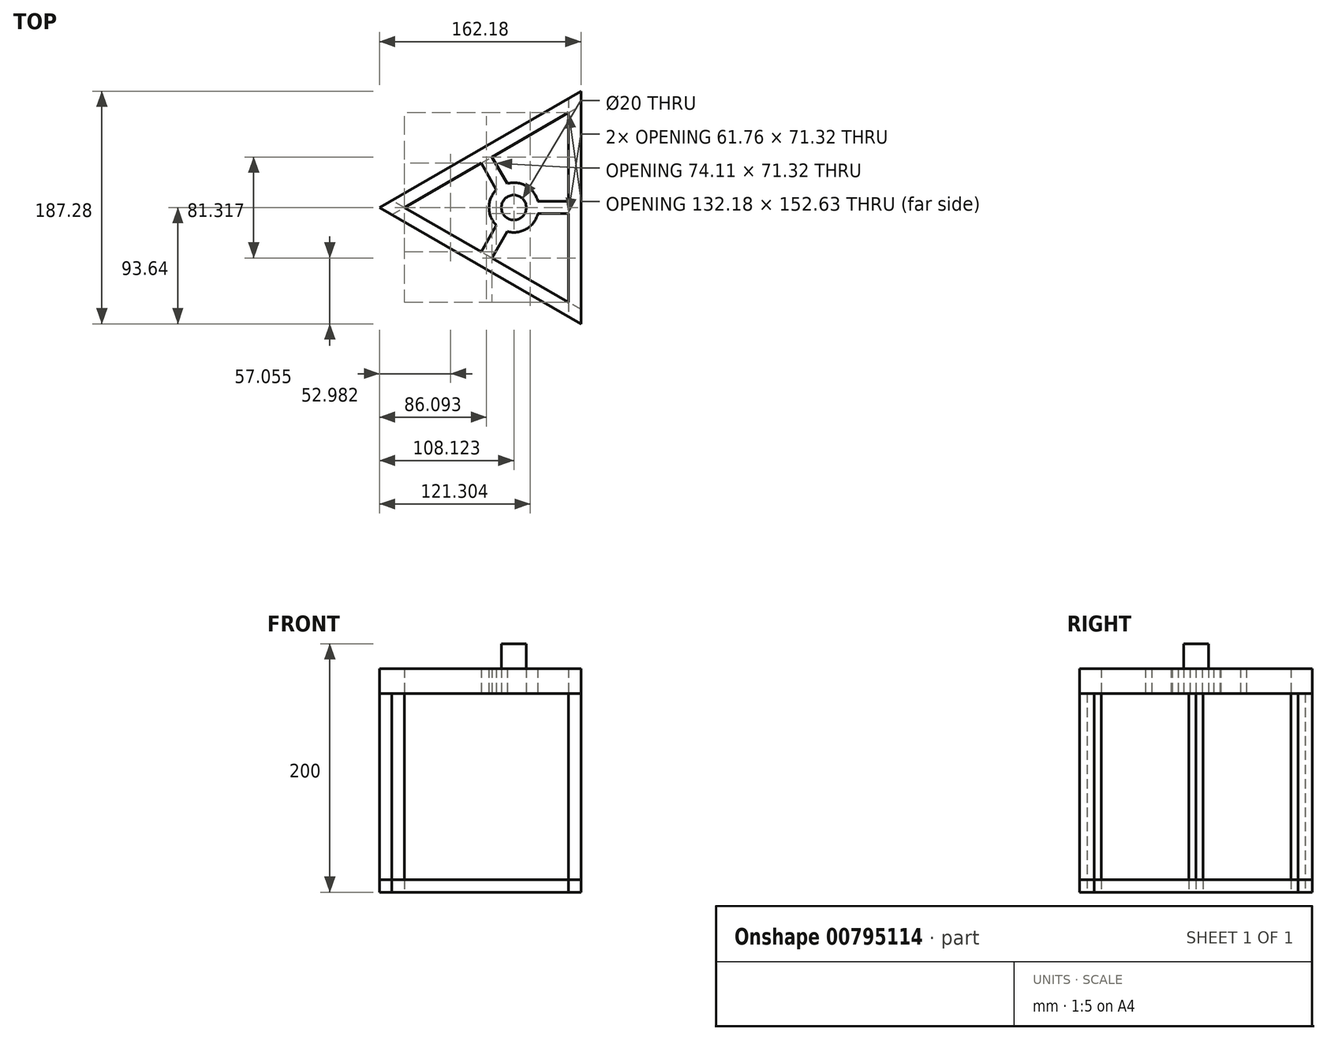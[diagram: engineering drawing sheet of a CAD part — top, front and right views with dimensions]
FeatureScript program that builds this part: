
annotation { "Feature Type Name" : "Feature", "Feature Type Description" : "" }
export const myFeature = defineFeature(function(context is Context, id is Id, definition is map)
    precondition{}
    {
        {
            var Q0;
            Q0=qCreatedBy(makeId("Top.planeOp"),FACE);
            var sketch = newSketch(context, id + "F0", { "sketchPlane" : qUnion([Q0])});
            skCircle(sketch, "E0.cCircle", {"center": v(0, 0) * mm, "radius": 54.06 * mm, "construction": true});
            skLineSegment(sketch, "E0.0", {"start": v(54.06, 93.64) * mm, "end": v(54.06, -93.64) * mm});
            skLineSegment(sketch, "E0.1", {"start": v(54.06, -93.64) * mm, "end": v(-108.12, 0) * mm});
            skLineSegment(sketch, "E0.2", {"start": v(-108.12, 0) * mm, "end": v(54.06, 93.64) * mm});
            skPoint(sketch, "E0.0.midPoint", {"position": v(54.06, 0) * mm});
            skLineSegment(sketch, "E1.0", {"start": v(44.06, 87.86) * mm, "end": v(44.06, -87.86) * mm});
            skLineSegment(sketch, "E2.0", {"start": v(-98.12, -5.77) * mm, "end": v(54.06, 82.1) * mm});
            skLineSegment(sketch, "E3.0", {"start": v(54.06, -82.1) * mm, "end": v(-98.12, 5.77) * mm});
            skCircle(sketch, "E4", {"center": v(0, 0) * mm, "radius": 8.55 * mm});
            skSolve(sketch);
        }
        {
            var Q0;
            {var subQ0=sQuery(id+"F0.wireOp",EDGE,"E2.0");var subQ1=sQuery(id+"F0.wireOp",EDGE,"E0.0");var subQ2=makeQuery(id+"F0.imprint","INTERSECT",VERTEX,{"derivedFrom":[subQ1,subQ0]});Q0=makeQuery(id+"F0.imprint","IMPRINT",FACE,{"disambiguationData":[TD([[makeQuery(id+"F0.imprint","IMPRINT",EDGE,{"disambiguationData":[TD([[subQ2,-1.0]])],"derivedFrom":subQ1}),-1.0]])]});}
            var Q1;
            {var subQ0=sQuery(id+"F0.wireOp",EDGE,"E0.2");var subQ1=sQuery(id+"F0.wireOp",EDGE,"E0.1");var subQ2=makeQuery(id+"F0.imprint","INTERSECT",VERTEX,{"derivedFrom":[subQ1,subQ0]});Q1=makeQuery(id+"F0.imprint","IMPRINT",FACE,{"disambiguationData":[TD([[makeQuery(id+"F0.imprint","IMPRINT",EDGE,{"disambiguationData":[TD([[subQ2,1.0]])],"derivedFrom":subQ1}),-1.0]])]});}
            var Q2;
            {var subQ0=sQuery(id+"F0.wireOp",EDGE,"E0.1");var subQ1=sQuery(id+"F0.wireOp",EDGE,"E0.0");var subQ2=makeQuery(id+"F0.imprint","INTERSECT",VERTEX,{"derivedFrom":[subQ1,subQ0]});Q2=makeQuery(id+"F0.imprint","IMPRINT",FACE,{"disambiguationData":[TD([[makeQuery(id+"F0.imprint","IMPRINT",EDGE,{"disambiguationData":[TD([[subQ2,1.0]])],"derivedFrom":subQ1}),-1.0]])]});}
            var Q3;
            {var subQ0=sQuery(id+"F0.wireOp",EDGE,"E1.0");var subQ1=sQuery(id+"F0.wireOp",EDGE,"E0.2");var subQ2=makeQuery(id+"F0.imprint","INTERSECT",VERTEX,{"derivedFrom":[subQ1,subQ0]});Q3=makeQuery(id+"F0.imprint","IMPRINT",FACE,{"disambiguationData":[TD([[makeQuery(id+"F0.imprint","IMPRINT",EDGE,{"disambiguationData":[TD([[subQ2,1.0]])],"derivedFrom":subQ1}),-1.0]])]});}
            var Q4;
            {var subQ0=sQuery(id+"F0.wireOp",EDGE,"E0.2");var subQ1=sQuery(id+"F0.wireOp",EDGE,"E0.0");var subQ2=makeQuery(id+"F0.imprint","INTERSECT",VERTEX,{"derivedFrom":[subQ1,subQ0]});Q4=makeQuery(id+"F0.imprint","IMPRINT",FACE,{"disambiguationData":[TD([[makeQuery(id+"F0.imprint","IMPRINT",EDGE,{"disambiguationData":[TD([[subQ2,-1.0]])],"derivedFrom":subQ1}),-1.0]])]});}
            var Q5;
            {var subQ0=sQuery(id+"F0.wireOp",EDGE,"E1.0");var subQ1=sQuery(id+"F0.wireOp",EDGE,"E0.1");var subQ2=makeQuery(id+"F0.imprint","INTERSECT",VERTEX,{"derivedFrom":[subQ1,subQ0]});Q5=makeQuery(id+"F0.imprint","IMPRINT",FACE,{"disambiguationData":[TD([[makeQuery(id+"F0.imprint","IMPRINT",EDGE,{"disambiguationData":[TD([[subQ2,-1.0]])],"derivedFrom":subQ1}),-1.0]])]});}
            extrude(context, id + "F1", {"entities" : qUnion([Q0, Q1, Q2, Q3, Q4, Q5]), "depth" : 10 * mm, "offsetDistance" : 25 * mm});
        }
        {
            var Q0;
            Q0=makeQuery(id+"F0.imprint","IMPRINT",FACE,{"disambiguationData":[TD([[makeQuery(id+"F0.imprint","IMPRINT",EDGE,{"derivedFrom":sQuery(id+"F0.wireOp",EDGE,"E4")}),-1.0]])]});
            var sketch = newSketch(context, id + "F2", { "sketchPlane" : qUnion([Q0])});
            skLineSegment(sketch, "E5.0", {"start": v(48.05, 93.64) * mm, "end": v(48.05, 82.1) * mm});
            skLineSegment(sketch, "E5.1", {"start": v(48.05, -93.64) * mm, "end": v(38.05, -87.86) * mm});
            skLineSegment(sketch, "E5.2", {"start": v(-114.13, 0) * mm, "end": v(-104.13, 5.77) * mm});
            skPoint(sketch, "E5.0.midPoint", {"position": v(48.05, 0) * mm});
            skLineSegment(sketch, "E6.0", {"start": v(38.05, 87.86) * mm, "end": v(38.05, 76.32) * mm});
            skLineSegment(sketch, "E7.0", {"start": v(-104.13, -5.77) * mm, "end": v(-94.13, 0) * mm});
            skLineSegment(sketch, "E8.0", {"start": v(48.05, -82.1) * mm, "end": v(38.05, -76.32) * mm});
            skLineSegment(sketch, "E9.trimOffspring", {"start": v(-94.13, 0) * mm, "end": v(-104.13, 5.77) * mm});
            skLineSegment(sketch, "E10.trimOffspring", {"start": v(-104.13, -5.77) * mm, "end": v(-114.13, 0) * mm});
            skLineSegment(sketch, "E11.trimOffspring", {"start": v(38.05, 76.32) * mm, "end": v(48.05, 82.1) * mm});
            skLineSegment(sketch, "E12.trimOffspring", {"start": v(38.05, 87.86) * mm, "end": v(48.05, 93.64) * mm});
            skLineSegment(sketch, "E13.trimOffspring", {"start": v(38.05, -76.32) * mm, "end": v(38.05, -87.86) * mm});
            skLineSegment(sketch, "E14.trimOffspring", {"start": v(48.05, -82.1) * mm, "end": v(48.05, -93.64) * mm});
            skPoint(sketch, "E5.cCircle.center.orphan", {"position": v(-6, 0) * mm});
            skSolve(sketch);
        }
        {
            var Q0;
            Q0=makeQuery(id+"F2.imprint","IMPRINT",FACE,{"disambiguationData":[TD([[makeQuery(id+"F2.imprint","IMPRINT",EDGE,{"derivedFrom":sQuery(id+"F2.wireOp",EDGE,"E5.0")}),-1.0]])]});
            var Q1;
            Q1=makeQuery(id+"F2.imprint","IMPRINT",FACE,{"disambiguationData":[TD([[makeQuery(id+"F2.imprint","IMPRINT",EDGE,{"derivedFrom":sQuery(id+"F2.wireOp",EDGE,"E5.1")}),-1.0]])]});
            var Q2;
            Q2=makeQuery(id+"F2.imprint","IMPRINT",FACE,{"disambiguationData":[TD([[makeQuery(id+"F2.imprint","IMPRINT",EDGE,{"derivedFrom":sQuery(id+"F2.wireOp",EDGE,"E5.2")}),-1.0]])]});
            extrude(context, id + "F3", {"entities" : qUnion([Q0, Q1, Q2]), "depth" : 160 * mm, "offsetDistance" : 25 * mm});
        }
        {
            var Q0;
            Q0=qCreatedBy(makeId("Top.planeOp"),FACE);
            var sketch = newSketch(context, id + "F4", { "sketchPlane" : qUnion([Q0])});
            skCircle(sketch, "E15.cCircle", {"center": v(-6, 0) * mm, "radius": 54.06 * mm, "construction": true});
            skLineSegment(sketch, "E15.0", {"start": v(48.05, 93.64) * mm, "end": v(48.05, -93.64) * mm});
            skLineSegment(sketch, "E15.1", {"start": v(48.05, -93.64) * mm, "end": v(-114.13, 0) * mm});
            skLineSegment(sketch, "E15.2", {"start": v(-114.13, 0) * mm, "end": v(48.05, 93.64) * mm});
            skPoint(sketch, "E15.0.midPoint", {"position": v(48.05, 0) * mm});
            skLineSegment(sketch, "E16.0", {"start": v(38.05, 87.86) * mm, "end": v(38.05, -87.86) * mm});
            skLineSegment(sketch, "E17.0", {"start": v(-104.13, -5.77) * mm, "end": v(48.05, 82.1) * mm});
            skLineSegment(sketch, "E18.0", {"start": v(48.05, -82.1) * mm, "end": v(-104.13, 5.77) * mm});
            skCircle(sketch, "E19", {"center": v(-6, 0) * mm, "radius": 10 * mm});
            skCircle(sketch, "E20.0", {"center": v(-6, 0) * mm, "radius": 20 * mm});
            skLineSegment(sketch, "E21.0", {"start": v(13.36, -5) * mm, "end": v(38.05, -5) * mm});
            skLineSegment(sketch, "E22.0", {"start": v(13.36, 5) * mm, "end": v(38.05, 5) * mm});
            skLineSegment(sketch, "E23.0", {"start": v(-20.02, -14.27) * mm, "end": v(-32.37, -35.66) * mm});
            skPoint(sketch, "E24.orphan", {"position": v(-28.04, 38.16) * mm});
            skLineSegment(sketch, "E25.trimOffspring", {"start": v(-20.02, 14.27) * mm, "end": v(-32.37, 35.66) * mm});
            skLineSegment(sketch, "E26.trimOffspring", {"start": v(-11.36, 19.27) * mm, "end": v(-23.7, 40.66) * mm});
            skLineSegment(sketch, "E27.trimOffspring", {"start": v(-11.36, -19.27) * mm, "end": v(-23.7, -40.66) * mm});
            skPoint(sketch, "E28.end.orphan", {"position": v(-28.04, -38.16) * mm});
            skPoint(sketch, "E29.end.orphan", {"position": v(38.05, 0) * mm});
            skSolve(sketch);
        }
        {
            var Q0;
            Q0=makeQuery(id+"F4.imprint","IMPRINT",FACE,{"disambiguationData":[TD([[makeQuery(id+"F4.imprint","IMPRINT",EDGE,{"derivedFrom":sQuery(id+"F4.wireOp",EDGE,"E19")}),1.0]])]});
            extrude(context, id + "F5", {"entities" : qUnion([Q0]), "depth" : 40 * mm, "offsetDistance" : 25 * mm});
        }
        {
            var Q0;
            {var subQ0=sQuery(id+"F4.wireOp",EDGE,"E21.0");Q0=makeQuery(id+"F4.imprint","IMPRINT",FACE,{"disambiguationData":[TD([[makeQuery(id+"F4.imprint","IMPRINT",EDGE,{"derivedFrom":subQ0}),1.0]])]});}
            var Q1;
            {var subQ0=sQuery(id+"F4.wireOp",EDGE,"E15.2");var subQ1=sQuery(id+"F4.wireOp",EDGE,"E15.1");var subQ2=makeQuery(id+"F4.imprint","INTERSECT",VERTEX,{"derivedFrom":[subQ1,subQ0]});Q1=makeQuery(id+"F4.imprint","IMPRINT",FACE,{"disambiguationData":[TD([[makeQuery(id+"F4.imprint","IMPRINT",EDGE,{"disambiguationData":[TD([[subQ2,1.0]])],"derivedFrom":subQ1}),-1.0]])]});}
            var Q2;
            {var subQ0=sQuery(id+"F4.wireOp",EDGE,"E15.1");var subQ1=sQuery(id+"F4.wireOp",EDGE,"E15.0");var subQ2=makeQuery(id+"F4.imprint","INTERSECT",VERTEX,{"derivedFrom":[subQ1,subQ0]});Q2=makeQuery(id+"F4.imprint","IMPRINT",FACE,{"disambiguationData":[TD([[makeQuery(id+"F4.imprint","IMPRINT",EDGE,{"disambiguationData":[TD([[subQ2,1.0]])],"derivedFrom":subQ1}),-1.0]])]});}
            var Q3;
            {var subQ4=sQuery(id+"F4.wireOp",EDGE,"E17.0");var subQ5=sQuery(id+"F4.wireOp",EDGE,"E15.0");var subQ6=makeQuery(id+"F4.imprint","INTERSECT",VERTEX,{"derivedFrom":[subQ5,subQ4]});Q3=makeQuery(id+"F4.imprint","IMPRINT",FACE,{"disambiguationData":[TD([[makeQuery(id+"F4.imprint","IMPRINT",EDGE,{"disambiguationData":[TD([[subQ6,-1.0]])],"derivedFrom":subQ5}),-1.0]])]});}
            var Q4;
            {var subQ2=sQuery(id+"F4.wireOp",EDGE,"E16.0");var subQ4=sQuery(id+"F4.wireOp",EDGE,"E15.1");var subQ5=makeQuery(id+"F4.imprint","INTERSECT",VERTEX,{"derivedFrom":[subQ4,subQ2]});Q4=makeQuery(id+"F4.imprint","IMPRINT",FACE,{"disambiguationData":[TD([[makeQuery(id+"F4.imprint","IMPRINT",EDGE,{"disambiguationData":[TD([[subQ5,-1.0]])],"derivedFrom":subQ4}),-1.0]])]});}
            var Q5;
            {var subQ0=sQuery(id+"F4.wireOp",EDGE,"E15.2");var subQ1=sQuery(id+"F4.wireOp",EDGE,"E15.0");var subQ2=makeQuery(id+"F4.imprint","INTERSECT",VERTEX,{"derivedFrom":[subQ1,subQ0]});Q5=makeQuery(id+"F4.imprint","IMPRINT",FACE,{"disambiguationData":[TD([[makeQuery(id+"F4.imprint","IMPRINT",EDGE,{"disambiguationData":[TD([[subQ2,-1.0]])],"derivedFrom":subQ1}),-1.0]])]});}
            var Q6;
            {var subQ0=sQuery(id+"F4.wireOp",EDGE,"E25.trimOffspring");Q6=makeQuery(id+"F4.imprint","IMPRINT",FACE,{"disambiguationData":[TD([[makeQuery(id+"F4.imprint","IMPRINT",EDGE,{"derivedFrom":subQ0}),-1.0]])]});}
            var Q7;
            {var subQ0=sQuery(id+"F4.wireOp",EDGE,"E23.0");Q7=makeQuery(id+"F4.imprint","IMPRINT",FACE,{"disambiguationData":[TD([[makeQuery(id+"F4.imprint","IMPRINT",EDGE,{"derivedFrom":subQ0}),1.0]])]});}
            var Q8;
            Q8=makeQuery(id+"F4.imprint","IMPRINT",FACE,{"disambiguationData":[TD([[makeQuery(id+"F4.imprint","IMPRINT",EDGE,{"derivedFrom":sQuery(id+"F4.wireOp",EDGE,"E19")}),-1.0]])]});
            var Q9;
            {var subQ5=sQuery(id+"F4.wireOp",EDGE,"E16.0");var subQ6=sQuery(id+"F4.wireOp",EDGE,"E15.2");var subQ7=makeQuery(id+"F4.imprint","INTERSECT",VERTEX,{"derivedFrom":[subQ6,subQ5]});Q9=makeQuery(id+"F4.imprint","IMPRINT",FACE,{"disambiguationData":[TD([[makeQuery(id+"F4.imprint","IMPRINT",EDGE,{"disambiguationData":[TD([[subQ7,1.0]])],"derivedFrom":subQ6}),-1.0]])]});}
            extrude(context, id + "F6", {"entities" : qUnion([Q0, Q1, Q2, Q3, Q4, Q5, Q6, Q7, Q8, Q9]), "depth" : 20 * mm, "offsetDistance" : 25 * mm});
        }
        {
            var Q0;
            Q0=makeQuery(id+"F1.opExtrude","SWEPT_BODY",BODY,{"disambiguationData":[OSD([sQuery(id+"F0.wireOp",EDGE,"E0.0"),sQuery(id+"F0.wireOp",EDGE,"E0.1"),sQuery(id+"F0.wireOp",EDGE,"E0.2"),sQuery(id+"F0.wireOp",EDGE,"E1.0"),sQuery(id+"F0.wireOp",EDGE,"E2.0"),sQuery(id+"F0.wireOp",EDGE,"E3.0")])]});
            var Q1;
            Q1=makeQuery(id+"F1.opExtrude","CAP_VERTEX",VERTEX,{"disambiguationData":[OSD([sQuery(id+"F0.wireOp",EDGE,"E0.0"),sQuery(id+"F0.wireOp",EDGE,"E0.2")])],"isStart":true});
            var Q2;
            Q2=makeQuery(id+"F6.opExtrude","CAP_VERTEX",VERTEX,{"disambiguationData":[OSD([sQuery(id+"F4.wireOp",EDGE,"E15.0"),sQuery(id+"F4.wireOp",EDGE,"E15.2")])],"isStart":true});
            transform(context, id + "F7", {"entities" : qUnion([Q0]), "transformType" : TransformType.TRANSLATION_ENTITY, "oppositeDirectionEntity" : false, "transformLine" : qUnion([Q1, Q2]), "makeCopy" : false});
        }
        {
            var Q0;
            Q0=makeQuery(id+"F6.opExtrude","SWEPT_BODY",BODY,{"disambiguationData":[OSD([sQuery(id+"F4.wireOp",EDGE,"E15.0"),sQuery(id+"F4.wireOp",EDGE,"E15.1"),sQuery(id+"F4.wireOp",EDGE,"E15.2"),sQuery(id+"F4.wireOp",EDGE,"E16.0"),sQuery(id+"F4.wireOp",EDGE,"E17.0"),sQuery(id+"F4.wireOp",EDGE,"E18.0"),sQuery(id+"F4.wireOp",EDGE,"E19"),sQuery(id+"F4.wireOp",EDGE,"E20.0"),sQuery(id+"F4.wireOp",EDGE,"E21.0"),sQuery(id+"F4.wireOp",EDGE,"E22.0"),sQuery(id+"F4.wireOp",EDGE,"E23.0"),sQuery(id+"F4.wireOp",EDGE,"E25.trimOffspring"),sQuery(id+"F4.wireOp",EDGE,"E26.trimOffspring"),sQuery(id+"F4.wireOp",EDGE,"E27.trimOffspring")])]});
            var Q1;
            Q1=makeQuery(id+"F1.opExtrude","CAP_VERTEX",VERTEX,{"disambiguationData":[OSD([sQuery(id+"F0.wireOp",EDGE,"E0.0"),sQuery(id+"F0.wireOp",EDGE,"E0.2")])],"isStart":true});
            var Q2;
            Q2=makeQuery(id+"F3.opExtrude","CAP_VERTEX",VERTEX,{"disambiguationData":[OSD([sQuery(id+"F2.wireOp",EDGE,"E5.0"),sQuery(id+"F2.wireOp",EDGE,"E12.trimOffspring")])],"isStart":false});
            transform(context, id + "F8", {"entities" : qUnion([Q0]), "transformType" : TransformType.TRANSLATION_ENTITY, "oppositeDirectionEntity" : false, "transformLine" : qUnion([Q1, Q2]), "makeCopy" : false});
        }
        {
            var Q0;
            Q0=makeQuery(id+"F5.opExtrude","SWEPT_BODY",BODY,{"disambiguationData":[OSD([sQuery(id+"F4.wireOp",EDGE,"E19")])]});
            transform(context, id + "F9", {"entities" : qUnion([Q0]), "transformType" : TransformType.TRANSLATION_3D, "dx" : 0 * mm, "dy" : 0 * mm, "dz" : 160 * mm, "makeCopy" : false});
        }
    });
